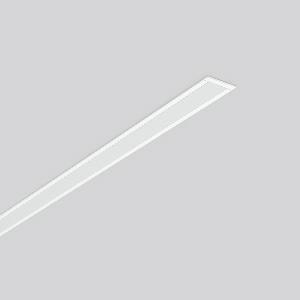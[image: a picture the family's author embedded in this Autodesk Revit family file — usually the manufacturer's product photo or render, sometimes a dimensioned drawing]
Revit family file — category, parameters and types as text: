
# Revit family: less_is_more_27_312176_002_8375
name_source: partatom
category: Lighting Fixtures
units: mm (PartAtom-declared; Revit-internal decimal feet)

## family parameters
Cut with Voids When Loaded = No
Host = Face
Light Source = No
Part Type = Normal
Room Calculation Point = No
Round Connector Dimension = Use Diameter
Shared = No

## types (1)
- LESS IS MORE 27 (1 x LED Modul 830, 1950 lm, 3000)
    Apparent Load = 29 VA
    CIE Flux Codes = 48 79 96 100 100
    Color Rendering = 80
    Color Temperature = 3000
    Default Elevation = 1800 mm
    Description = Series: LESS IS MORE 27
Recessed ceiling and wall luminaire with slim design. Housing: extruded aluminium profile, powder-coated. End cap aluminium powder-coated. Diffuser made of non-yellowing plastic (PMMA), opal. Suitable for Recessed ceiling mounting, wall (recessed). External driver with connecting cable. 
Colour: traffic white, matt (RAL 9016)
Length: 1014 mm
Width: 38 mm
Height: 2 mm
Cut-out length: 1006 mm
Cut-out width: 30 mm
Recess height: 45-60 mm
Luminaire: recess height: 37 mm
Lamp: LED
Socket: without socket
Colour temperature: 3000K
Colour rendering index (CRI): 82
System power: 29 W
Rated luminous flux: 1950 lm
Luminous efficiency: 67 lm/W
Control gear: Regulated power supply
Protection class: II
Type of protection: IP 20
    Height = 0 mm  [stored 0 ft]
    Lamp = 1 x LED Modul 830
    Lamp Light Flux = 1950 lm
    Lamp count = 1
    Length = 1014 mm
    Lifetime = 50000 h
    Luminous efficacy = 67 lm/W
    Manufacturer = RZB
    ModVariant = No
    Model = 312176.002
    Mounting Place = Ceiling, Wall
    Mounting Type = Recessed
    Number of Poles = 1
    OnlyDefault = Yes
    Power Factor = 1
    Product Name = LESS IS MORE 27
    Product group = Recessed LED linear luminaires
    ProductGroupID = 407
    Protection Class = Protection class II
    Protection Degree = IP 20
    RLX_Detail_Level = 1
    RLX_Emergency_Light_Flux = 0 lm
    RLX_Emergency_Type = 0
    RLX_Emergency_Type_DB = No
    RlxData = <blob elided: 21533 chars, md5=a7ed3ce7>
    Socket = socket
    Standby Power = 0 W
    System Light Flux = 1950 lm
    System Power = 29 W
    Type Comments = Product without accessories
    Type Image = 312176.002.jpg
    URL = http://relux.com
    VarID = ---
    Voltage = 230 V
    Voltage Range = 220-240 V
    Weight = 0.00 kg
    Width = 38 mm

note: [stored X ft] marks values corroborated as IEEE doubles in the binary element streams (Revit-internal decimal feet)

## geometry (parser evidence)
native form markers: Blend x4, Sweep x12
no freeform markers — native parametric forms only
